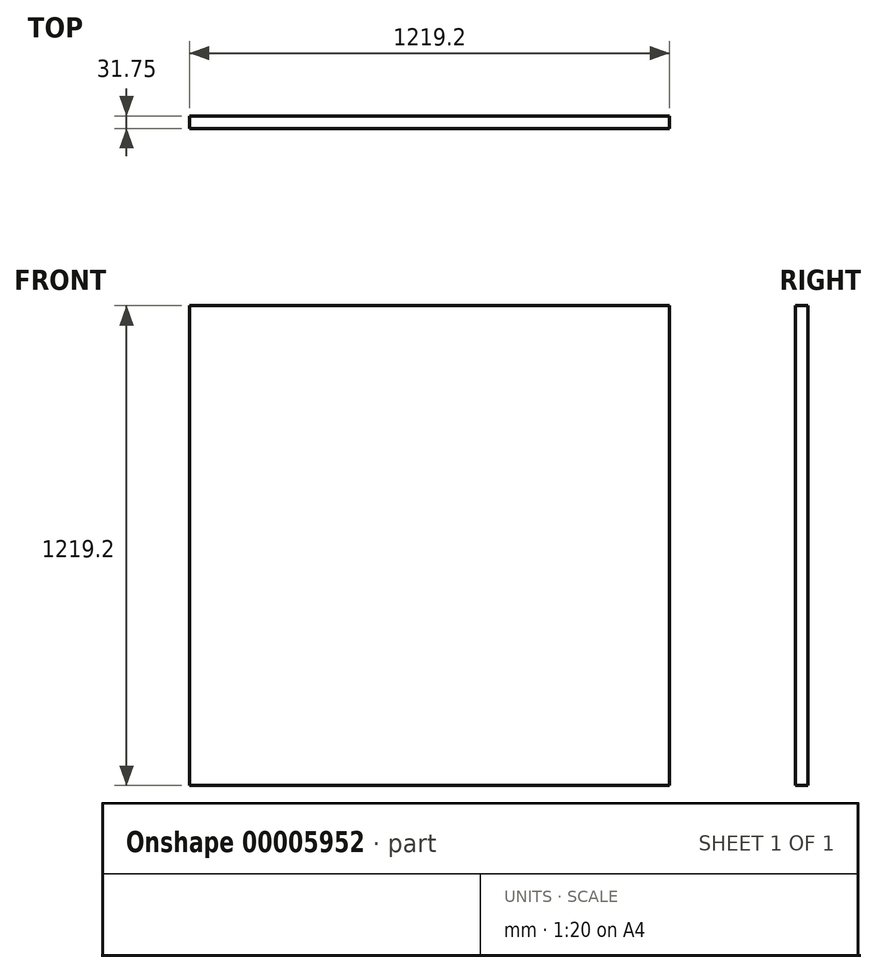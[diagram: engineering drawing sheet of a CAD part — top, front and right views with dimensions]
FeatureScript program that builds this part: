
annotation { "Feature Type Name" : "Feature", "Feature Type Description" : "" }
export const myFeature = defineFeature(function(context is Context, id is Id, definition is map)
    precondition{}
    {
        {
            var Q0;
            Q0=qCreatedBy(makeId("Front.planeOp"),FACE);
            var sketch = newSketch(context, id + "F0", { "sketchPlane" : qUnion([Q0])});
            skLineSegment(sketch, "E0.bottom", {"start": v(-617.72, 505.98) * mm, "end": v(601.48, 505.98) * mm});
            skLineSegment(sketch, "E0.top", {"start": v(-617.72, -713.22) * mm, "end": v(601.48, -713.22) * mm});
            skLineSegment(sketch, "E0.left", {"start": v(-617.72, 505.98) * mm, "end": v(-617.72, -713.22) * mm});
            skLineSegment(sketch, "E0.right", {"start": v(601.48, 505.98) * mm, "end": v(601.48, -713.22) * mm});
            skSolve(sketch);
        }
        {
            var Q0;
            Q0=qSketchRegion(id+"F0",true);
            extrude(context, id + "F1", {"entities" : qUnion([Q0]), "depth" : 31.75 * mm});
        }
    });
